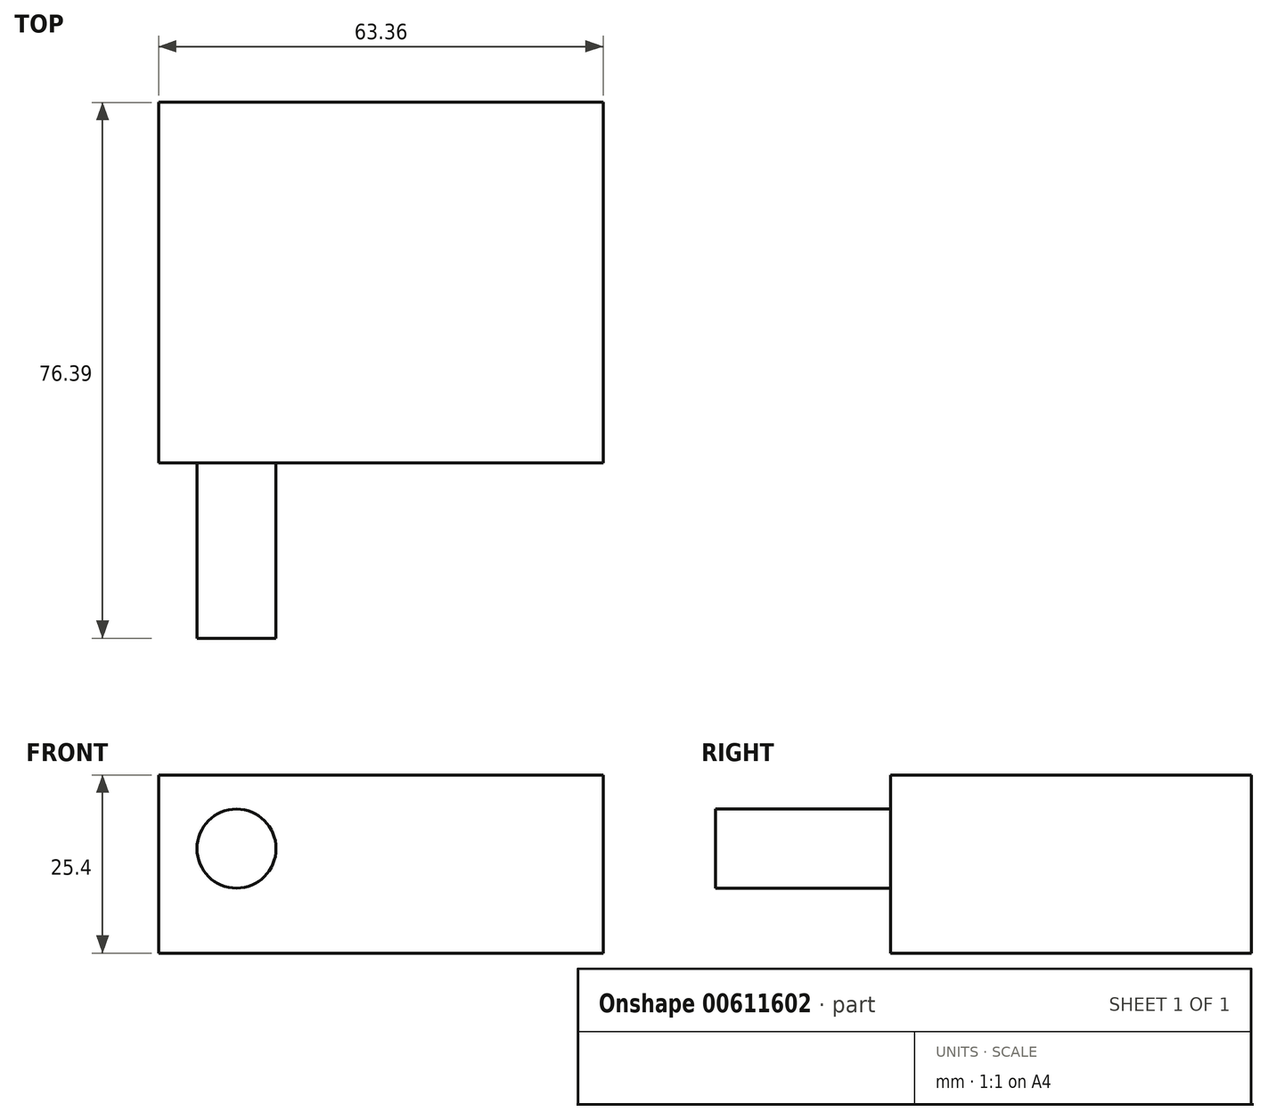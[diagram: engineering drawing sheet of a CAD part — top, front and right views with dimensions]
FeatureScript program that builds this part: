
annotation { "Feature Type Name" : "Feature", "Feature Type Description" : "" }
export const myFeature = defineFeature(function(context is Context, id is Id, definition is map)
    precondition{}
    {
        {
            var Q0;
            Q0=qCreatedBy(makeId("Top.planeOp"),FACE);
            var sketch = newSketch(context, id + "F0", { "sketchPlane" : qUnion([Q0])});
            skLineSegment(sketch, "E0.bottom", {"start": v(-28.47, 24.38) * mm, "end": v(34.9, 24.38) * mm});
            skLineSegment(sketch, "E0.top", {"start": v(-28.47, -27.01) * mm, "end": v(34.9, -27.01) * mm});
            skLineSegment(sketch, "E0.left", {"start": v(-28.47, 24.38) * mm, "end": v(-28.47, -27.01) * mm});
            skLineSegment(sketch, "E0.right", {"start": v(34.9, 24.38) * mm, "end": v(34.9, -27.01) * mm});
            skSolve(sketch);
        }
        {
            var Q0;
            Q0=makeQuery(id+"F0.imprint","IMPRINT",FACE,{"disambiguationData":[TD([[makeQuery(id+"F0.imprint","IMPRINT",EDGE,{"derivedFrom":sQuery(id+"F0.wireOp",EDGE,"E0.bottom")}),-1.0]])]});
            extrude(context, id + "F1", {"entities" : qUnion([Q0]), "depth" : 25.4 * mm, "offsetDistance" : 25.4 * mm});
        }
        {
            var Q0;
            Q0=makeQuery(id+"F1.opExtrude","SWEPT_FACE",FACE,{"disambiguationData":[OSD([sQuery(id+"F0.wireOp",EDGE,"E0.top")])]});
            var sketch = newSketch(context, id + "F2", { "sketchPlane" : qUnion([Q0])});
            skCircle(sketch, "E1", {"center": v(-17.37, 14.9) * mm, "radius": 5.64 * mm});
            skSolve(sketch);
        }
        {
            var Q0;
            Q0 = qSketchRegion(id + "F2", true);
            extrude(context, id + "F3", {"entities" : qUnion([Q0]), "operationType" : NewBodyOperationType.ADD, "depth" : 25 * mm, "offsetDistance" : 25 * mm});
        }
    });
